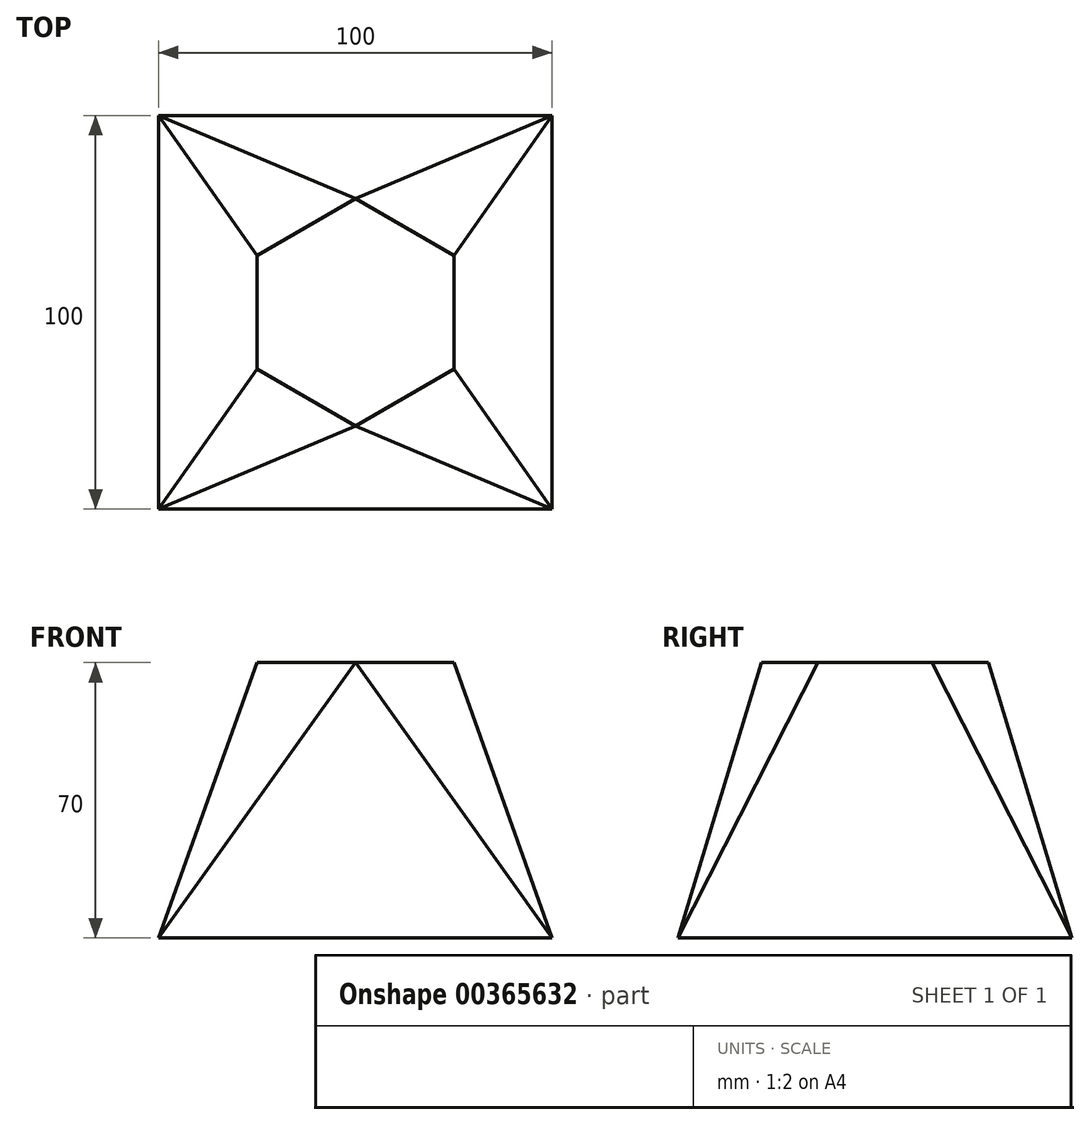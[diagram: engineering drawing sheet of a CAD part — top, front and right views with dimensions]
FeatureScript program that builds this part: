
annotation { "Feature Type Name" : "Feature", "Feature Type Description" : "" }
export const myFeature = defineFeature(function(context is Context, id is Id, definition is map)
    precondition{}
    {
        {
            var Q0;
            Q0=qCreatedBy(makeId("Top.planeOp"),FACE);
            var sketch = newSketch(context, id + "F0", { "sketchPlane" : qUnion([Q0])});
            skLineSegment(sketch, "E0.bottom", {"start": v(50, 50) * mm, "end": v(-50, 50) * mm});
            skLineSegment(sketch, "E0.top", {"start": v(50, -50) * mm, "end": v(-50, -50) * mm});
            skLineSegment(sketch, "E0.left", {"start": v(50, 50) * mm, "end": v(50, -50) * mm});
            skLineSegment(sketch, "E0.right", {"start": v(-50, 50) * mm, "end": v(-50, -50) * mm});
            skPoint(sketch, "E0.middle", {"position": v(0, 0) * mm});
            skSolve(sketch);
        }
        {
            var Q0;
            Q0=qCreatedBy(makeId("Top.planeOp"),FACE);
            cPlane(context, id + "F1", {"entities" : qUnion([Q0]), "cplaneType" : CPlaneType.OFFSET, "offset" : 70 * mm, "width" : 150 * mm, "height" : 150 * mm});
        }
        {
            var Q0;
            Q0=qCreatedBy(id+"F1.planeOp",FACE);
            var sketch = newSketch(context, id + "F2", { "sketchPlane" : qUnion([Q0])});
            skCircle(sketch, "E1.cCircle", {"center": v(0, 0) * mm, "radius": 25 * mm, "construction": true});
            skLineSegment(sketch, "E1.0", {"start": v(25, 14.43) * mm, "end": v(25, -14.43) * mm});
            skLineSegment(sketch, "E1.1", {"start": v(25, -14.43) * mm, "end": v(0, -28.87) * mm});
            skLineSegment(sketch, "E1.2", {"start": v(0, -28.87) * mm, "end": v(-25, -14.43) * mm});
            skLineSegment(sketch, "E1.3", {"start": v(-25, -14.43) * mm, "end": v(-25, 14.43) * mm});
            skLineSegment(sketch, "E1.4", {"start": v(-25, 14.43) * mm, "end": v(0, 28.87) * mm});
            skLineSegment(sketch, "E1.5", {"start": v(0, 28.87) * mm, "end": v(25, 14.43) * mm});
            skPoint(sketch, "E1.0.midPoint", {"position": v(25, 0) * mm});
            skLineSegment(sketch, "E2", {"start": v(-25, -14.43) * mm, "end": v(25, -14.43) * mm});
            skLineSegment(sketch, "E3", {"start": v(-25, 14.43) * mm, "end": v(25, 14.43) * mm});
            skSolve(sketch);
        }
        {
            var Q0;
            Q0=makeQuery(id+"F2.imprint","IMPRINT",FACE,{"disambiguationData":[TD([[makeQuery(id+"F2.imprint","IMPRINT",EDGE,{"derivedFrom":sQuery(id+"F2.wireOp",EDGE,"E1.0")}),-1.0]])]});
            var Q1;
            Q1=makeQuery(id+"F0.imprint","IMPRINT",FACE,{"disambiguationData":[TD([[makeQuery(id+"F0.imprint","IMPRINT",EDGE,{"derivedFrom":sQuery(id+"F0.wireOp",EDGE,"E0.bottom")}),1.0]])]});
            loft(context, id + "F3", {"sheetProfilesArray" : [{ "sheetProfileEntities" : qUnion([Q0]) }, { "sheetProfileEntities" : qUnion([Q1]) }]});
        }
        {
            var Q1;
            Q1=makeQuery(id+"F2.imprint","IMPRINT",FACE,{"disambiguationData":[TD([[makeQuery(id+"F2.imprint","IMPRINT",EDGE,{"derivedFrom":sQuery(id+"F2.wireOp",EDGE,"E1.1")}),-1.0]])]});
            var Q2;
            Q2=makeQuery(id+"F3.opLoft","MID_CAP_VERTEX",VERTEX,{"disambiguationData":[OSD([sQuery(id+"F0.wireOp",EDGE,"E0.top"),sQuery(id+"F0.wireOp",EDGE,"E0.right")])],"capPos":1.0});
            loft(context, id + "F4", {"operationType" : NewBodyOperationType.ADD, "sheetProfilesArray" : [{ "sheetProfileEntities" : qUnion([Q1]) }, { "sheetProfileEntities" : qUnion([Q2]) }]});
        }
        {
            var Q1;
            Q1=makeQuery(id+"F2.imprint","IMPRINT",FACE,{"disambiguationData":[TD([[makeQuery(id+"F2.imprint","IMPRINT",EDGE,{"derivedFrom":sQuery(id+"F2.wireOp",EDGE,"E1.1")}),-1.0]])]});
            var Q2;
            Q2=makeQuery(id+"F3.opLoft","MID_CAP_VERTEX",VERTEX,{"disambiguationData":[OSD([sQuery(id+"F0.wireOp",EDGE,"E0.top"),sQuery(id+"F0.wireOp",EDGE,"E0.left")])],"capPos":1.0});
            loft(context, id + "F5", {"operationType" : NewBodyOperationType.ADD, "sheetProfilesArray" : [{ "sheetProfileEntities" : qUnion([Q1]) }, { "sheetProfileEntities" : qUnion([Q2]) }]});
        }
        {
            var Q1;
            Q1=makeQuery(id+"F4.opLoft","SWEPT_FACE",FACE,{"disambiguationData":[OSD([sQuery(id+"F2.wireOp",EDGE,"E1.0"),sQuery(id+"F2.wireOp",EDGE,"E1.1"),sQuery(id+"F2.wireOp",EDGE,"E1.2"),sQuery(id+"F2.wireOp",EDGE,"E2")])]});
            var Q2;
            Q2=makeQuery(id+"F5.opLoft","SWEPT_FACE",FACE,{"disambiguationData":[OSD([sQuery(id+"F2.wireOp",EDGE,"E1.1"),sQuery(id+"F2.wireOp",EDGE,"E1.2"),sQuery(id+"F2.wireOp",EDGE,"E1.3"),sQuery(id+"F2.wireOp",EDGE,"E2")])]});
            var Q3;
            Q3=makeQuery(id+"F3.opLoft","MID_CAP_EDGE",EDGE,{"disambiguationData":[OSD([sQuery(id+"F0.wireOp",EDGE,"E0.top"),sQuery(id+"F0.wireOp",EDGE,"E0.left"),sQuery(id+"F0.wireOp",EDGE,"E0.right")])],"capPos":1.0});
            loft(context, id + "F6", {"operationType" : NewBodyOperationType.ADD, "addGuides" : true, "sheetProfilesArray" : [{ "sheetProfileEntities" : qUnion([Q1]) }, { "sheetProfileEntities" : qUnion([Q2]) }], "guidesArray" : [{ "guideEntities" : qUnion([Q3]), "guideDerivativeType" : LoftGuideDerivativeType.DEFAULT, "guideDerivativeMagnitude" : 1 }]});
        }
        {
            var Q1;
            Q1=makeQuery(id+"F2.imprint","IMPRINT",FACE,{"disambiguationData":[TD([[makeQuery(id+"F2.imprint","IMPRINT",EDGE,{"derivedFrom":sQuery(id+"F2.wireOp",EDGE,"E1.4")}),-1.0]])]});
            var Q2;
            Q2=makeQuery(id+"F3.opLoft","MID_CAP_VERTEX",VERTEX,{"disambiguationData":[OSD([sQuery(id+"F0.wireOp",EDGE,"E0.bottom"),sQuery(id+"F0.wireOp",EDGE,"E0.left")])],"capPos":1.0});
            loft(context, id + "F7", {"operationType" : NewBodyOperationType.ADD, "sheetProfilesArray" : [{ "sheetProfileEntities" : qUnion([Q1]) }, { "sheetProfileEntities" : qUnion([Q2]) }]});
        }
        {
            var Q1;
            Q1=makeQuery(id+"F2.imprint","IMPRINT",FACE,{"disambiguationData":[TD([[makeQuery(id+"F2.imprint","IMPRINT",EDGE,{"derivedFrom":sQuery(id+"F2.wireOp",EDGE,"E1.4")}),-1.0]])]});
            var Q2;
            Q2=makeQuery(id+"F3.opLoft","MID_CAP_VERTEX",VERTEX,{"disambiguationData":[OSD([sQuery(id+"F0.wireOp",EDGE,"E0.bottom"),sQuery(id+"F0.wireOp",EDGE,"E0.right")])],"capPos":1.0});
            loft(context, id + "F8", {"operationType" : NewBodyOperationType.ADD, "sheetProfilesArray" : [{ "sheetProfileEntities" : qUnion([Q1]) }, { "sheetProfileEntities" : qUnion([Q2]) }]});
        }
        {
            var Q1;
            Q1=makeQuery(id+"F7.opLoft","SWEPT_FACE",FACE,{"disambiguationData":[OSD([sQuery(id+"F2.wireOp",EDGE,"E1.3"),sQuery(id+"F2.wireOp",EDGE,"E1.4"),sQuery(id+"F2.wireOp",EDGE,"E1.5"),sQuery(id+"F2.wireOp",EDGE,"E3")])]});
            var Q2;
            Q2=makeQuery(id+"F8.opLoft","SWEPT_FACE",FACE,{"disambiguationData":[OSD([sQuery(id+"F2.wireOp",EDGE,"E1.0"),sQuery(id+"F2.wireOp",EDGE,"E1.4"),sQuery(id+"F2.wireOp",EDGE,"E1.5"),sQuery(id+"F2.wireOp",EDGE,"E3")])]});
            var Q3;
            Q3=makeQuery(id+"F3.opLoft","MID_CAP_EDGE",EDGE,{"disambiguationData":[OSD([sQuery(id+"F0.wireOp",EDGE,"E0.bottom"),sQuery(id+"F0.wireOp",EDGE,"E0.left"),sQuery(id+"F0.wireOp",EDGE,"E0.right")])],"capPos":1.0});
            loft(context, id + "F9", {"operationType" : NewBodyOperationType.ADD, "addGuides" : true, "sheetProfilesArray" : [{ "sheetProfileEntities" : qUnion([Q1]) }, { "sheetProfileEntities" : qUnion([Q2]) }], "guidesArray" : [{ "guideEntities" : qUnion([Q3]), "guideDerivativeType" : LoftGuideDerivativeType.DEFAULT, "guideDerivativeMagnitude" : 1 }]});
        }
    });
